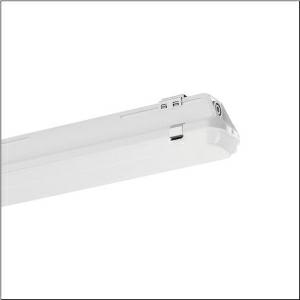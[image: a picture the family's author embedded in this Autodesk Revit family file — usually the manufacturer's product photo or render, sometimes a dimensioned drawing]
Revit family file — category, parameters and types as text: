
# Revit family: monsun_r__12_51fp20dp460h_a65e
name_source: partatom
category: Lighting Fixtures
units: mm (PartAtom-declared; Revit-internal decimal feet)

## family parameters
Cut with Voids When Loaded = No
Host = Face
Light Source = No
Part Type = Normal
Room Calculation Point = No
Round Connector Dimension = Use Diameter
Shared = No

## types (1)
- --- (1 x LED, 5450 lm, 34.6 W, 4000K)
    Apparent Load = 35 VA
    CIE Flux Codes = 45 75 93 94 100
    Color Rendering = 80
    Color Temperature = 4000K
    Default Elevation = 1800 mm
    Description = Monsun® 12, damp-proof luminaire, chain hanger, primary optical cover: enclosure, of PC, light emission: direct distribution, primary light characteristic: symmetric, installation type: suspended mounting, surface-mounted, horizontal mounting, vertical mounting, LED rated luminous flux: 5.450 lm, light colour: 840, colour temperature: 4000K, control gear: ECG DALI, with terminal, 5-pole, max. 2.5mm², mains connection: 220..240V, AC, 50/60Hz, rated input power: 35W, luminaire housing, of glass-fibre reinforced polyester, uncoated, bright grey, length: 1.590 mm, width: 90 mm, height: 88mm, clip for enclosure, of stainless steel (V2A), ceiling mounting element, of stainless steel (V2A), chain hanger, of stainless steel (V2A), protection rating (complete): IP66, insulation class (complete): insulation class I (protective earthing), certification: CE, ENEC, VDE, protection symbol: D, impact resistance: IK08, permissible ambient temperature for indoor applications: -35..+40°C, standard: EN 50419, EN 60598-2-1, no direct snow, no direct sun, no direct rain, for indoor or canopied outdoor use, corresponds to IFS (International Featured Standards) requirements for safety and quality in the food industry, packaging unit: 1 piece
    Height = 89 mm
    Lamp = 1 x LED
    Lamp Light Flux = 5450 lm
    Lamp Power = 34.6 W
    Lamp count = 1
    Length = 1590 mm
    Luminous efficacy = 158 lm/W
    Manufacturer = Siteco
    ModVariant = No
    Model = 51FP20DP460H
    Mounting Place = Ceiling
    Mounting Type = Pendant
    Number of Poles = 1
    OnlyDefault = Yes
    Power Factor = 1
    Product Name = Monsun® 12
    Product group = damp-proof luminaire | ceiling pendant
    ProductGroupID = 908
    Protection Class = Protection class I
    Protection Degree = IP 66
    RLX_Detail_Level = 1
    RlxData = <blob elided: 92349 chars, md5=ac575f3b>
    Socket = socket
    Standby Power = 0 W
    System Light Flux = 5450 lm
    System Power = 35 W
    Type Comments = factory setting: luminous flux: 100 % | dim-lin: 254 | 232 mA
    Type Image = l_1004748.jpg
    URL = http://relux.com
    VarID = @adj_133967
    Voltage = 0 V
    Weight = 0.00 kg
    Width = 90 mm

## geometry (parser evidence)
native form markers: Blend x4, Sweep x14
no freeform markers — native parametric forms only
